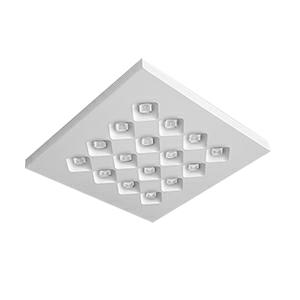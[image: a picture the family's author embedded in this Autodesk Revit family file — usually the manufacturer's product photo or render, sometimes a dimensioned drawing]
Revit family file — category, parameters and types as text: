
# Revit family: 3f_filippi_-_3f_diagon_soft_ugr_3f_filippi_-_23814_a0686_-_3f_diagon_25w-840_dali_soft_ugr_596x596___corn_plaf__de76
name_source: partatom
category: Lighting Fixtures
units: mm (PartAtom-declared; Revit-internal decimal feet)

## family parameters
Cut with Voids When Loaded = No
Host = Face
Light Source = No
Part Type = Normal
Room Calculation Point = No
Round Connector Dimension = Use Diameter
Shared = No

## types (1)
- 3F Filippi - 3F Dìagon Soft UGR (1 x LED, 3679 lm, 28 W, 4000 K)
    Apparent Load = 28 VA
    Approval mark = CE
    CIE Flux Codes = 59 92 100 100 100
    Color Rendering = 80
    Color Temperature = 4000 K
    Control Gear = Electronic transformer
    Default Elevation = 1800 mm
    Description = ILLUMINOTECHNICAL
Luminous efficiency 100% (DLOR 100%, ULOR 0%).
Initial luminous flux of the luminaire 3679 lm.
Direct symmetric distribution.
Installation Interdistance Transv.D = 1.23 x hu - Long.D = 1.23 x hu.
Average luminance <3000 cd/m² for radial angles >65°.
Tabular UGR (CIE 117 - 4H-8H; S=0.25H; 70/50/20): RUG 18.7 - 18.7.
Beam angle: 102° - 101°.
Luminous efficacy 131 lm/W.
Lifetime (L95/B10): 30000 h. (tq+25°C)
Lifetime (L90/B10): 50000 h. (tq+25°C)
Lifetime (L80/B10): 80000 h. (tq+25°C)
Lifetime (L75/B10): 100000 h. (tq+25°C)
Sudden decreased luminous flux after 50000 hours: 0% (C0).
Photobiological safety in compliance with IEC/TR 62778: RG0 risk exempt, (IEC 62471).
In compliance with IEC/EN 62722-2-1 - IEC/EN 62717 standards.

SOURCE
Squared LED module 25W/840.
Energy efficiency class (UE 2019/2020 - UE 2019/2015): C.
CIE 13.3 Colour rendering index: CRI >80 (R9 <50%).
IES TM-30 Fidelity Index: Rf = 84 Rg = 95.
CCT nominal colour temperature 4000 K.
Colour initial tolerance (MacAdam): SDCM 3.

MECHANICAL
Housing in hot-galvanised steel, painted in white polyester.
Honeycombed diagonal screen in white anti-glare polycarbonate.
Opal methacrylate (PMMA) rhomboid lenses with differentiated, engraved and prismatic surfaces for diffused, soft lighting and excellent visual comfort.
Luminaire with limited surface temperature. - D - (EN 60598-2-24)
Dimensions: 600x600 mm, height 40 mm. Weight 6.22 kg.
IP43 protection degree for exposed part, IP20 for recessed part.
Mechanical strength to impacts IK06 (1 joule).
Glow-wire test resistance 650°C.

ELECTRICAL
Halogen Free DALI-2, PUSH-DIM, electronic wiring 230V-50/60Hz, power factor 0.95 at full load, THD <25%, constant output current, class I, 1 driver, 1 DALI addresse.
Power of the luminaire 28 W.
ENEC - CE.
SAFE FLICKER: PstLM=<1 and SVM=<0.4 (IEC TR 61547-1 and IEC TR 63158), to ensure a more comfortable and safe light.
Luminaire compliant with EN 60598-2-22 for power supply from a centralised emergency system CPSS (Central Power Supply System), not incorporated in the luminaire - high risk areas excluded. The default power and flux are 100% in AC and 15% in DC.
Ambient temperature from 0°C to +25°C.
Temperature class T6 max 85°C.
Quick connection.
Relative humidity UR: <85%.

INSTALLATION
Ceiling.
Height only 40 mm.
All accessories dedicated to this product are available on the Catalog and on our website www.3F-Filippi.com.

ACCESSORIES
A0686 - 596x596 Diagon frame for Ceiling installation.

APPLICATIONS
Environments: staterooms, with VDTs, offices.
Environments with exacting visual tasks, where diffused soft light for optimum visual comfort is required.

LIGHT MANAGEMENT
Recommended minimum setting: 10%.
The device, equipped with DALI-2 driver, can be controlled manually with 3F Easy Dim technology or automatically/manually with 3F Smart Dimming technology and/or centralised DALI systems.
DALI-2 certification guarantees interoperability with other devices with the same certification.
In electrical systems without a regulation system (manual or automatic) and DALI bus, a suitable jumper must be made on the DA-DA terminals of the appliance.

WARNING
Luminaire designed for disposal/recycling at end-of-life.
Replaceable (LED only) light source by a professional. Replaceable control gear by a professional.
    Height = 0 mm  [stored 0 ft]
    Lamp = 1 x LED
    Lamp Light Flux = 3679 lm
    Lamp Power = 28 W
    Lamp count = 1
    Length = 600 mm
    Lifetime = 50000 h
    Luminous efficacy = 131 lm/W
    Manufacturer = 3F Filippi
    ModVariant = No
    Model = 3F Filippi - 23814+A0686 - 3F Diagon 25W-840 DALI SOFT UGR 596x596 + Corn.plaf.
    Mounting Place = Ceiling
    Mounting Type = Recessed
    Number of Poles = 1
    OnlyDefault = Yes
    Power Factor = 1
    Product Name = 3F Filippi - 3F Dìagon Soft UGR
    Product group = recessed luminaire
    ProductGroupID = 4
    Protection Class = Protection class I
    Protection Degree = IP 20
    RLX_Detail_Level = 1
    RLX_Emergency_Light_Flux = 0 lm
    RLX_Emergency_Type = 0
    RLX_Emergency_Type_DB = No
    RlxData = <blob elided: 97641 chars, md5=c3a37819>
    Socket = socket
    Standby Power = 0 W
    System Light Flux = 3679 lm
    System Power = 28 W
    Type Comments = Product without accessories
    Type Image = 3ffilippi_3f_diagon__a0686.jpg
    URL = http://relux.com
    VarID = ---
    Voltage = 0 V
    Weight = 0.00 kg
    Width = 600 mm

note: [stored X ft] marks values corroborated as IEEE doubles in the binary element streams (Revit-internal decimal feet)

## geometry (parser evidence)
native form markers: Blend x4, Sweep x10
no freeform markers — native parametric forms only
